# Revit family: Legrand Distribution enclosure XL³ 6300-4000
name_source: partatom
category: Equipement électrique
units: mm (PartAtom-declared; Revit-internal decimal feet)

## family parameters
Basée sur le plan de construction = Non
Configuration du panneau = Deux colonnes, circuits au sein
Cote de connecteur circulaire = Utiliser le diamètre
Couper avec des vides une fois chargée = Non
Numéro OmniClass = 23.80.30.11.17
Partagée = Non
Point de calcul de pièce = Non
Titre OmniClass = Distribution Boards and Control Panels
Toujours verticalement = Oui
Type d'élément = Tableau de raccordement

## types (15) — shared parameters
Fabricant = Legrand
Finish = powder coated
Form of separation up to (until) = 4b
General Conditions of Use = https://export.legrand.com
ICW (until) = 110
IK without door = 07
IP without door = 30
Material = Steel
Modèle = XL³ 4000
RAL = 7035
zero-valued in all types: Elévation par défaut

## per-type parameters (varying)
| type | IK with door | IN max (A) | IP with door | URL | depth (mm) | door | height (mm) | width (mm) |
| 020504-020500-020514-020554 | 08 | 4000 | 55 | https://www.legrand.fr | 475 mm  [stored 1.5584 ft] | Oui | 2000 mm  [stored 6.56168 ft] | 725 mm  [stored 2.37861 ft] |
| 020504-020850-020514-020861 | 08 | 4000 | 55 | https://www.legrand.fr | 475 mm  [stored 1.5584 ft] | Oui | 2200 mm | 725 mm  [stored 2.37861 ft] |
| 020505-020500-020515-020554 | 08 | 4000 | 55 | https://www.legrand.fr | 725 mm  [stored 2.37861 ft] | Oui | 2000 mm  [stored 6.56168 ft] | 725 mm  [stored 2.37861 ft] |
| 020505-020850-020515-020861 | 08 | 4000 | 55 | https://www.legrand.fr | 725 mm  [stored 2.37861 ft] | Oui | 2200 mm | 725 mm  [stored 2.37861 ft] |
| 020506-020500-020516-020554 | 08 | 4000 | 55 | https://www.legrand.fr | 975 mm  [stored 3.19882 ft] | Oui | 2000 mm  [stored 6.56168 ft] | 725 mm  [stored 2.37861 ft] |
| 020506-020850-020516-020861 | 08 | 4000 | 55 | https://www.legrand.fr | 975 mm  [stored 3.19882 ft] | Oui | 2200 mm | 725 mm  [stored 2.37861 ft] |
| 020507-020500-020517-020554 | 08 | 4000 | 55 | https://www.legrand.fr | 475 mm  [stored 1.5584 ft] | Oui | 2000 mm  [stored 6.56168 ft] | 975 mm  [stored 3.19882 ft] |
| 020507-020850-020517-020861 | 08 | 4000 | 55 | https://www.legrand.fr
https://www.legrand.fr | 475 mm  [stored 1.5584 ft] | Oui | 2200 mm | 975 mm  [stored 3.19882 ft] |
| 020508-020500-020518-020554 | 08 | 4000 | 55 | https://www.legrand.fr | 725 mm  [stored 2.37861 ft] | Oui | 2000 mm  [stored 6.56168 ft] | 975 mm  [stored 3.19882 ft] |
| 020508-020850-020518-020861 | 08 | 4000 | 55 | https://www.legrand.fr | 725 mm  [stored 2.37861 ft] | Oui | 2200 mm | 975 mm  [stored 3.19882 ft] |
| 020509-020500-020519-020554 | 08 | 4000 | 55 | https://www.legrand.fr | 975 mm  [stored 3.19882 ft] | Oui | 2000 mm  [stored 6.56168 ft] | 975 mm  [stored 3.19882 ft] |
| 020509-020850-020519-020861 | 08 | 4000 | 55 | https://www.legrand.fr | 975 mm  [stored 3.19882 ft] | Oui | 2200 mm | 975 mm  [stored 3.19882 ft] |
| 021133-021136-021130 |  | 6300 |  | https://www.legrand.fr | 475 mm  [stored 1.5584 ft] | Non | 2200 mm | 1425 mm  [stored 4.6752 ft] |
| 021134-021136-021131 |  | 6300 |  | https://www.legrand.fr | 725 mm  [stored 2.37861 ft] | Non | 2200 mm | 1425 mm  [stored 4.6752 ft] |
| 021135-021136-021132 |  | 6300 |  | https://www.legrand.fr | 975 mm  [stored 3.19882 ft] | Non | 2200 mm | 1425 mm  [stored 4.6752 ft] |

note: [stored X ft] marks values corroborated as IEEE doubles in the binary element streams (Revit-internal decimal feet)
